# Revit family: Electronics_Communication_Talkaphone_AOR-IP-Station_Flush-Mounted
name_source: partatom
category: Telephone Devices
units: mm (PartAtom-declared; Revit-internal decimal feet)

## family parameters
Cut with Voids When Loaded = No
Host = Face
Maintain Annotation Orientation = No
OmniClass Number = 23.37.27.17
Part Type = Normal
Room Calculation Point = No
Round Connector Dimension = Use Diameter
Shared = No

## types (1)
- Area of Rescue IP Station, Flush Mounted
    Assembly Code = D5030300
    Communication = Full duplex two-way hands-free communication
    Connection = RJ45 Ethernet
    Construction = #4 brushed 304 stainless steel faceplate, 0.09 in. (2.2mm)
    Default Elevation = 48 "
    Depth = 2.75 "
    Description = THIS FLUSH MOUNTE AOR IP CALL STATION IS AN INDOOR, HANDS FREE ADA-COMPLIANT COMMUNICATION ENDPOINT FOR USE WITH AN IP AOR COMMAND UNIT IN AN AREA OF RESCUE ASSISTANCE.
    Digital Capacity = Up to 90-digits for each of five (5) phone numbers
    Edition number = 1
    Environment = For indoor use
    Height = 8.23 "
    Keynote = 27 30 00
    Manufacturer = Talkaphone
    Model = AOR-IP-CSE-FM
    Mounting = Flush mount
    Operating Temperature = -40ºF to +140ºF (-40ºC to +60ºC)
    Power Source = Power over Ethernet (IEEE 802.3af). Ethernet switch must include a power backup system in the event of power loss.
    Product Guid = 36f7c7d9-2c1d-404e-a557-5dc1d3b3a112
    Product Material = Talkaphone - Stainless Steel
    Product data url = https://www.bimobject.com
    Programming = Programming and configuration through Windows-based application. All programming is stored on non-volatile flash memory.
    Relative Humidity = Up to 95% non-condensing
    URL = https://www.talkaphone.com
    Warranty = 5-year limited warranty
    Width = 4.75 "
    Wiring = Minimum Cat5e. If required, fire resistive CI/CIC Ethernet cable is supported.
    “On Time” = Programmable for no limit or from 1 to 9 minutes in 1-minute increments

## geometry (parser evidence)
native form markers: Sweep x2
no freeform markers — native parametric forms only
